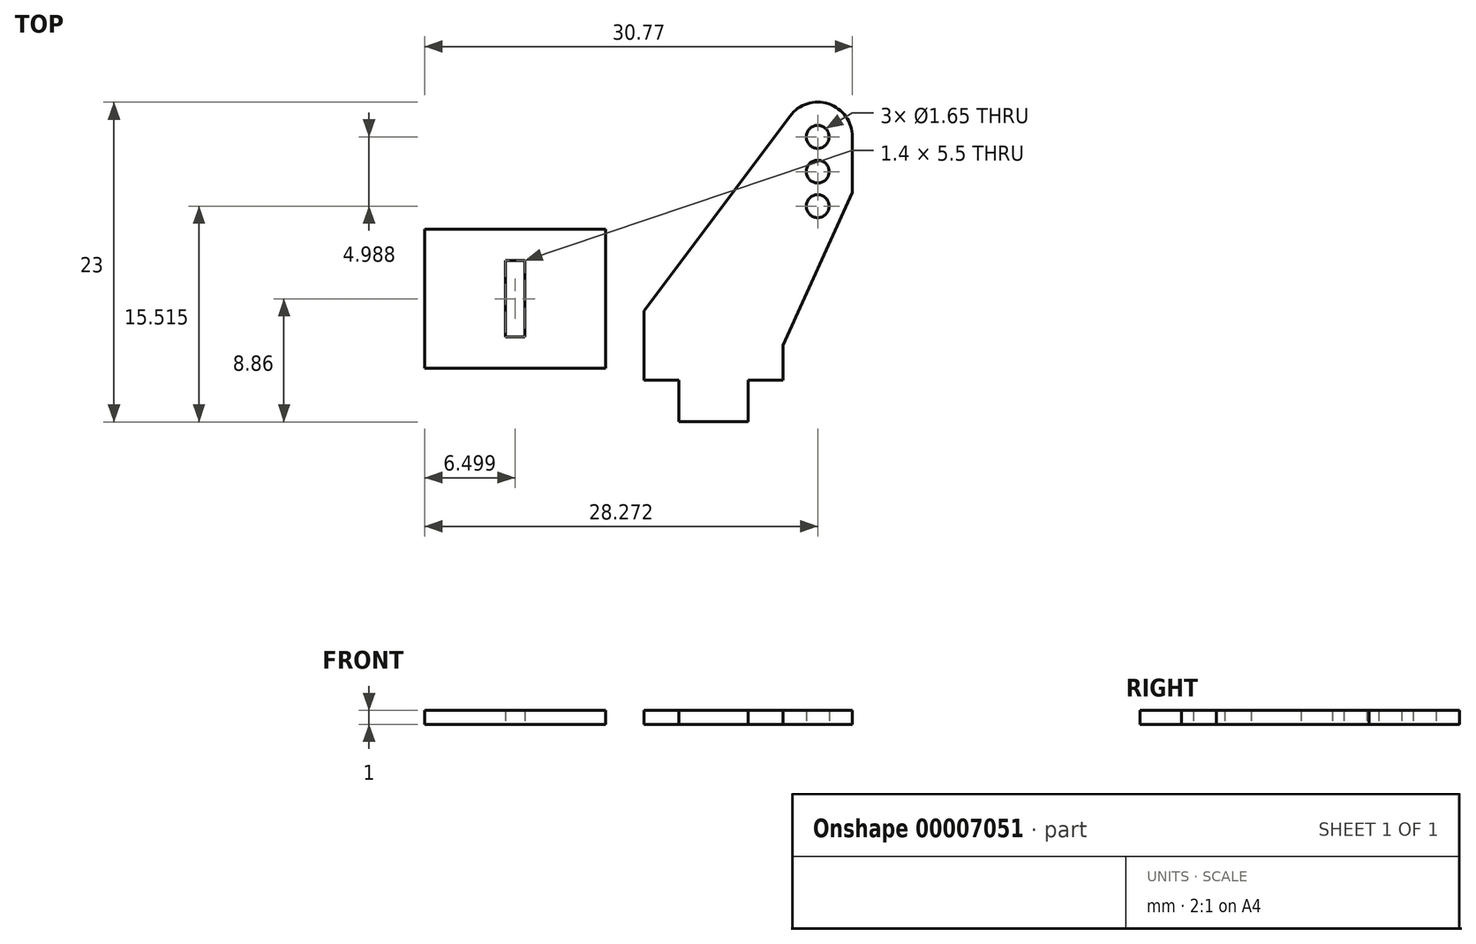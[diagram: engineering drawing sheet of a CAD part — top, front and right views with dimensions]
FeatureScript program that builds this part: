
annotation { "Feature Type Name" : "Feature", "Feature Type Description" : "" }
export const myFeature = defineFeature(function(context is Context, id is Id, definition is map)
    precondition{}
    {
        {
            var Q0;
            Q0=qCreatedBy(makeId("Top.planeOp"),FACE);
            var sketch = newSketch(context, id + "F0", { "sketchPlane" : qUnion([Q0])});
            skLineSegment(sketch, "E0.bottom", {"start": v(-39.9, 32.8) * mm, "end": v(-26.9, 32.8) * mm});
            skLineSegment(sketch, "E0.top", {"start": v(-39.9, 22.8) * mm, "end": v(-26.9, 22.8) * mm});
            skLineSegment(sketch, "E0.left", {"start": v(-39.9, 32.8) * mm, "end": v(-39.9, 22.8) * mm});
            skLineSegment(sketch, "E0.right", {"start": v(-26.9, 32.8) * mm, "end": v(-26.9, 22.8) * mm});
            skLineSegment(sketch, "E1.bottom", {"start": v(-21.63, 21.94) * mm, "end": v(-16.63, 21.94) * mm});
            skLineSegment(sketch, "E1.top", {"start": v(-21.63, 18.94) * mm, "end": v(-16.63, 18.94) * mm});
            skLineSegment(sketch, "E1.left", {"start": v(-21.63, 21.94) * mm, "end": v(-21.63, 18.94) * mm});
            skLineSegment(sketch, "E1.right", {"start": v(-16.63, 21.94) * mm, "end": v(-16.63, 18.94) * mm});
            skLineSegment(sketch, "E2", {"start": v(-16.63, 21.94) * mm, "end": v(-14.13, 21.94) * mm});
            skLineSegment(sketch, "E3", {"start": v(-21.63, 21.94) * mm, "end": v(-24.13, 21.94) * mm});
            skLineSegment(sketch, "E4", {"start": v(-24.13, 21.94) * mm, "end": v(-24.13, 26.94) * mm});
            skPoint(sketch, "E5.endSnap0", {"position": v(-11.63, 41.94) * mm});
            skLineSegment(sketch, "E6", {"start": v(-9.13, 39.44) * mm, "end": v(-9.13, 35.44) * mm});
            skLineSegment(sketch, "E7", {"start": v(-14.13, 21.94) * mm, "end": v(-14.13, 24.44) * mm});
            skLineSegment(sketch, "E8", {"start": v(-14.13, 24.44) * mm, "end": v(-9.13, 35.44) * mm});
            skLineSegment(sketch, "E9", {"start": v(-24.13, 26.94) * mm, "end": v(-13.63, 40.94) * mm});
            skArc(sketch, "E10", {"start": v(-9.13, 39.44) * mm, "mid": v(-10.84, 41.81) * mm, "end": v(-13.63, 40.94) * mm});
            skCircle(sketch, "E11", {"center": v(-11.63, 39.44) * mm, "radius": 0.82 * mm});
            skCircle(sketch, "E12", {"center": v(-11.63, 36.94) * mm, "radius": 0.82 * mm});
            skCircle(sketch, "E13", {"center": v(-11.63, 34.45) * mm, "radius": 0.82 * mm});
            skLineSegment(sketch, "E14", {"start": v(-33.4, 32.8) * mm, "end": v(-33.4, 37.21) * mm, "construction": true});
            skLineSegment(sketch, "E15", {"start": v(-33.4, 37.21) * mm, "end": v(-34.1, 37.21) * mm, "construction": true});
            skLineSegment(sketch, "E16", {"start": v(-33.4, 37.21) * mm, "end": v(-32.9, 37.21) * mm, "construction": true});
            skLineSegment(sketch, "E17", {"start": v(-39.9, 32.8) * mm, "end": v(-39.9, 30.55) * mm, "construction": true});
            skLineSegment(sketch, "E18", {"start": v(-34.1, 37.21) * mm, "end": v(-34.1, 19.73) * mm, "construction": true});
            skLineSegment(sketch, "E19", {"start": v(-39.9, 30.55) * mm, "end": v(-34.1, 30.55) * mm, "construction": true});
            skLineSegment(sketch, "E20.bottom", {"start": v(-34.1, 30.55) * mm, "end": v(-32.7, 30.55) * mm});
            skLineSegment(sketch, "E20.top", {"start": v(-34.1, 25.05) * mm, "end": v(-32.7, 25.05) * mm});
            skLineSegment(sketch, "E20.left", {"start": v(-34.1, 30.55) * mm, "end": v(-34.1, 25.05) * mm});
            skLineSegment(sketch, "E20.right", {"start": v(-32.7, 30.55) * mm, "end": v(-32.7, 25.05) * mm});
            skSolve(sketch);
        }
        {
            var Q0;
            Q0=makeQuery(id+"F0.imprint","IMPRINT",FACE,{"disambiguationData":[TD([[makeQuery(id+"F0.imprint","IMPRINT",EDGE,{"derivedFrom":sQuery(id+"F0.wireOp",EDGE,"E0.bottom")}),-1.0]])]});
            var Q1;
            Q1=makeQuery(id+"F0.imprint","IMPRINT",FACE,{"disambiguationData":[TD([[makeQuery(id+"F0.imprint","IMPRINT",EDGE,{"derivedFrom":sQuery(id+"F0.wireOp",EDGE,"E1.bottom")}),1.0]])]});
            var Q2;
            Q2=makeQuery(id+"F0.imprint","IMPRINT",FACE,{"disambiguationData":[TD([[makeQuery(id+"F0.imprint","IMPRINT",EDGE,{"derivedFrom":sQuery(id+"F0.wireOp",EDGE,"E1.bottom")}),-1.0]])]});
            extrude(context, id + "F1", {"entities" : qUnion([Q0, Q1, Q2]), "depth" : 1 * mm});
        }
    });
